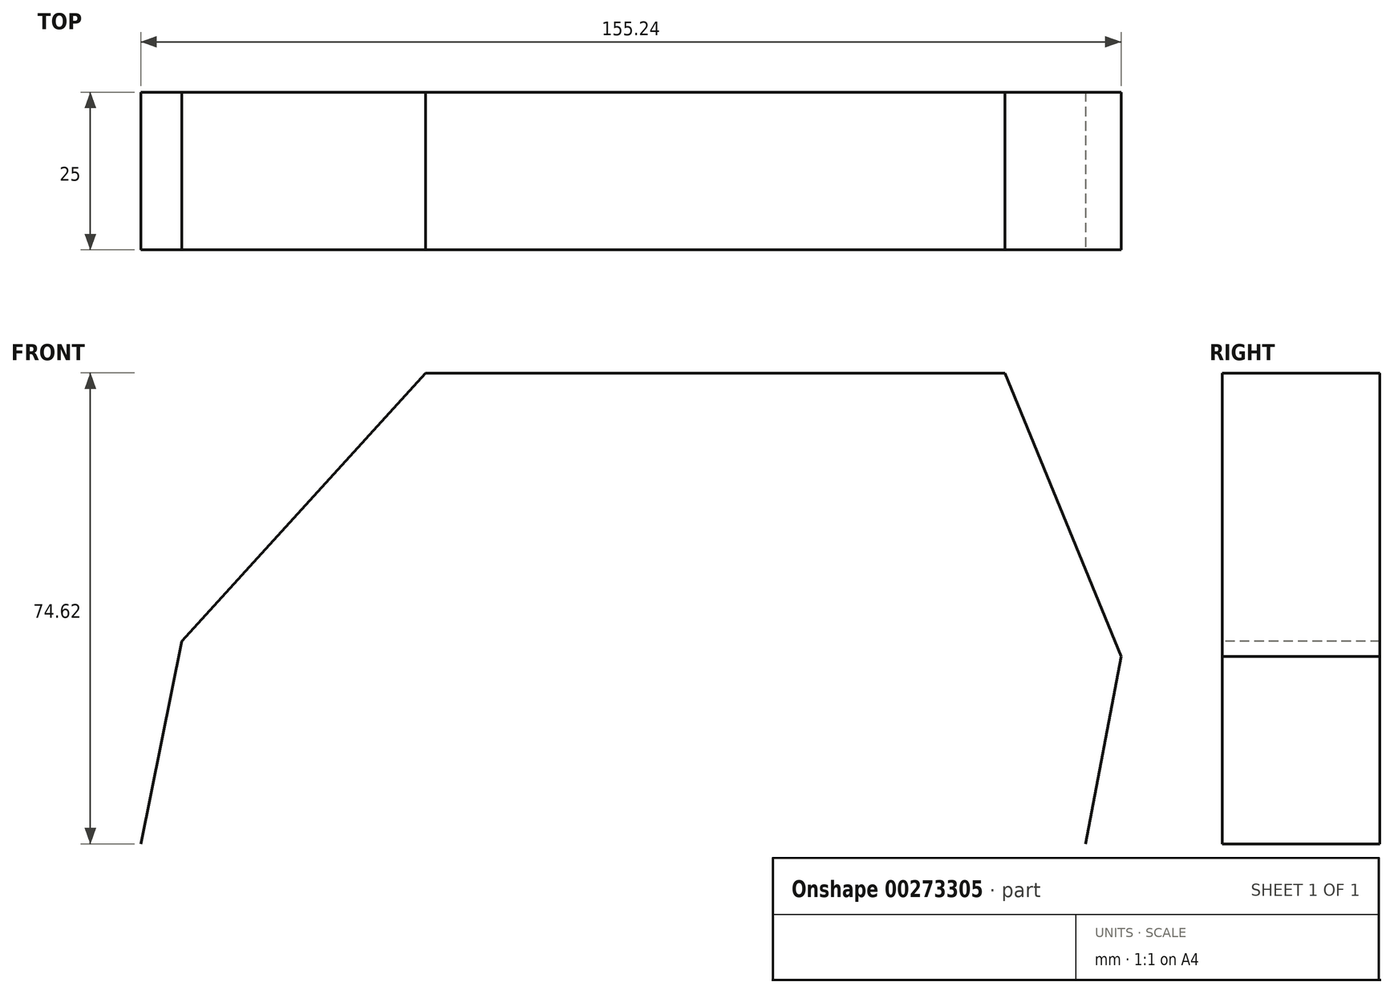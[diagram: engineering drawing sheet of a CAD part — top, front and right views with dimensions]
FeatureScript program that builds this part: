
annotation { "Feature Type Name" : "Feature", "Feature Type Description" : "" }
export const myFeature = defineFeature(function(context is Context, id is Id, definition is map)
    precondition{}
    {
        {
            var Q0;
            Q0=qCreatedBy(makeId("Front.planeOp"),FACE);
            var sketch = newSketch(context, id + "F0", { "sketchPlane" : qUnion([Q0])});
            skLineSegment(sketch, "E0", {"start": v(-75, 0) * mm, "end": v(74.62, 0) * mm});
            skLineSegment(sketch, "E1", {"start": v(74.62, 0) * mm, "end": v(44.73, 55.26) * mm});
            skLineSegment(sketch, "E2", {"start": v(44.73, 55.26) * mm, "end": v(-34.77, 55.26) * mm});
            skLineSegment(sketch, "E3", {"start": v(-34.77, 55.26) * mm, "end": v(-75, 0) * mm});
            skLineSegment(sketch, "E4", {"start": v(80.25, 29.7) * mm, "end": v(-68.49, 32.1) * mm});
            skLineSegment(sketch, "E5", {"start": v(61.83, 74.62) * mm, "end": v(44.73, 55.26) * mm});
            skLineSegment(sketch, "E6", {"start": v(61.83, 74.62) * mm, "end": v(-29.89, 74.62) * mm});
            skLineSegment(sketch, "E7", {"start": v(-29.89, 74.62) * mm, "end": v(-34.77, 55.26) * mm});
            skLineSegment(sketch, "E8", {"start": v(-29.89, 74.62) * mm, "end": v(-68.49, 32.1) * mm});
            skLineSegment(sketch, "E9", {"start": v(-68.49, 32.1) * mm, "end": v(-75, 0) * mm});
            skLineSegment(sketch, "E10", {"start": v(61.83, 74.62) * mm, "end": v(80.25, 29.7) * mm});
            skLineSegment(sketch, "E11", {"start": v(80.25, 29.7) * mm, "end": v(74.62, 0) * mm});
            skLineSegment(sketch, "E12", {"start": v(42.47, 18.98) * mm, "end": v(44.73, 18.41) * mm});
            skSolve(sketch);
        }
        {
            var Q0;
            Q0=sQuery(id+"F0.wireOp",EDGE,"E9");
            var Q1;
            Q1=sQuery(id+"F0.wireOp",EDGE,"E8");
            var Q2;
            Q2=sQuery(id+"F0.wireOp",EDGE,"E6");
            var Q3;
            Q3=sQuery(id+"F0.wireOp",EDGE,"E10");
            var Q4;
            Q4=sQuery(id+"F0.wireOp",EDGE,"E11");
            extrude(context, id + "F1", {"bodyType" : ToolBodyType.SURFACE, "surfaceEntities" : qUnion([Q0, Q1, Q2, Q3, Q4]), "depth" : 25 * mm});
        }
    });
